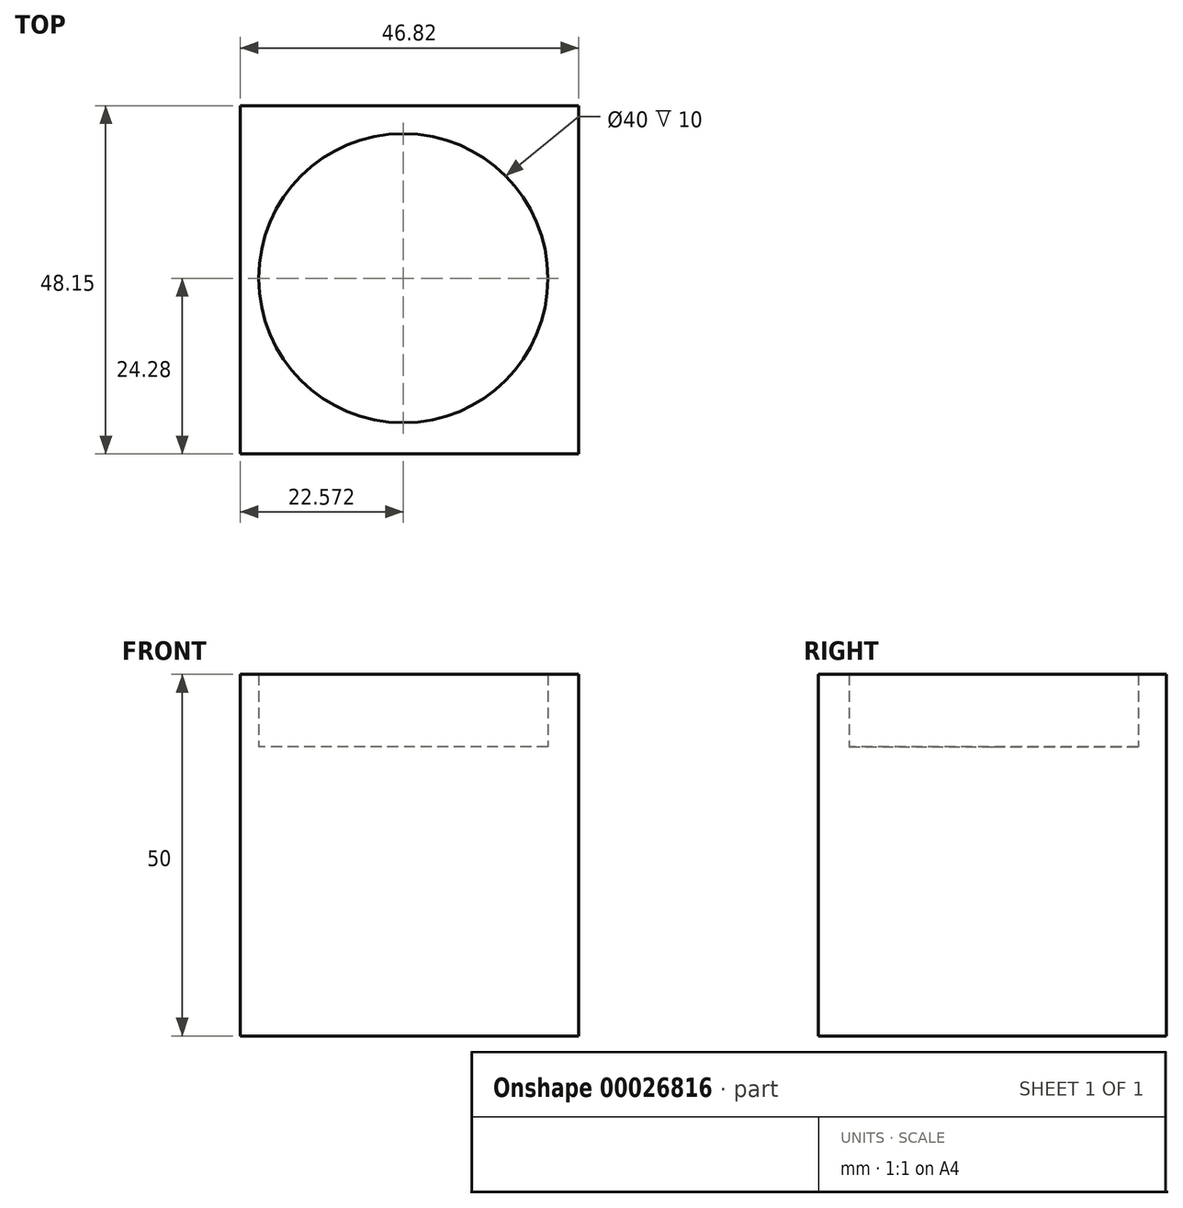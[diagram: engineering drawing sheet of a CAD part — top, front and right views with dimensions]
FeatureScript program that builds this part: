
annotation { "Feature Type Name" : "Feature", "Feature Type Description" : "" }
export const myFeature = defineFeature(function(context is Context, id is Id, definition is map)
    precondition{}
    {
        {
            var Q0;
            Q0=qCreatedBy(makeId("Top.planeOp"),FACE);
            var sketch = newSketch(context, id + "F0", { "sketchPlane" : qUnion([Q0])});
            skLineSegment(sketch, "E0.bottom", {"start": v(-11.35, 4.4) * mm, "end": v(35.47, 4.4) * mm});
            skLineSegment(sketch, "E0.top", {"start": v(-11.35, -43.74) * mm, "end": v(35.47, -43.74) * mm});
            skLineSegment(sketch, "E0.left", {"start": v(-11.35, 4.4) * mm, "end": v(-11.35, -43.74) * mm});
            skLineSegment(sketch, "E0.right", {"start": v(35.47, 4.4) * mm, "end": v(35.47, -43.74) * mm});
            skCircle(sketch, "E1", {"center": v(11.22, -19.46) * mm, "radius": 20 * mm});
            skSolve(sketch);
        }
        {
            var Q0;
            Q0=makeQuery(id+"F0.imprint","IMPRINT",FACE,{"disambiguationData":[TD([[makeQuery(id+"F0.imprint","IMPRINT",EDGE,{"derivedFrom":sQuery(id+"F0.wireOp",EDGE,"E1")}),1.0]])]});
            extrude(context, id + "F1", {"entities" : qUnion([Q0]), "depth" : 40 * mm});
        }
        {
            var Q0;
            Q0=makeQuery(id+"F0.imprint","IMPRINT",FACE,{"disambiguationData":[TD([[makeQuery(id+"F0.imprint","IMPRINT",EDGE,{"derivedFrom":sQuery(id+"F0.wireOp",EDGE,"E0.bottom")}),-1.0]])]});
            extrude(context, id + "F2", {"entities" : qUnion([Q0]), "operationType" : NewBodyOperationType.ADD, "depth" : 50 * mm});
        }
    });
